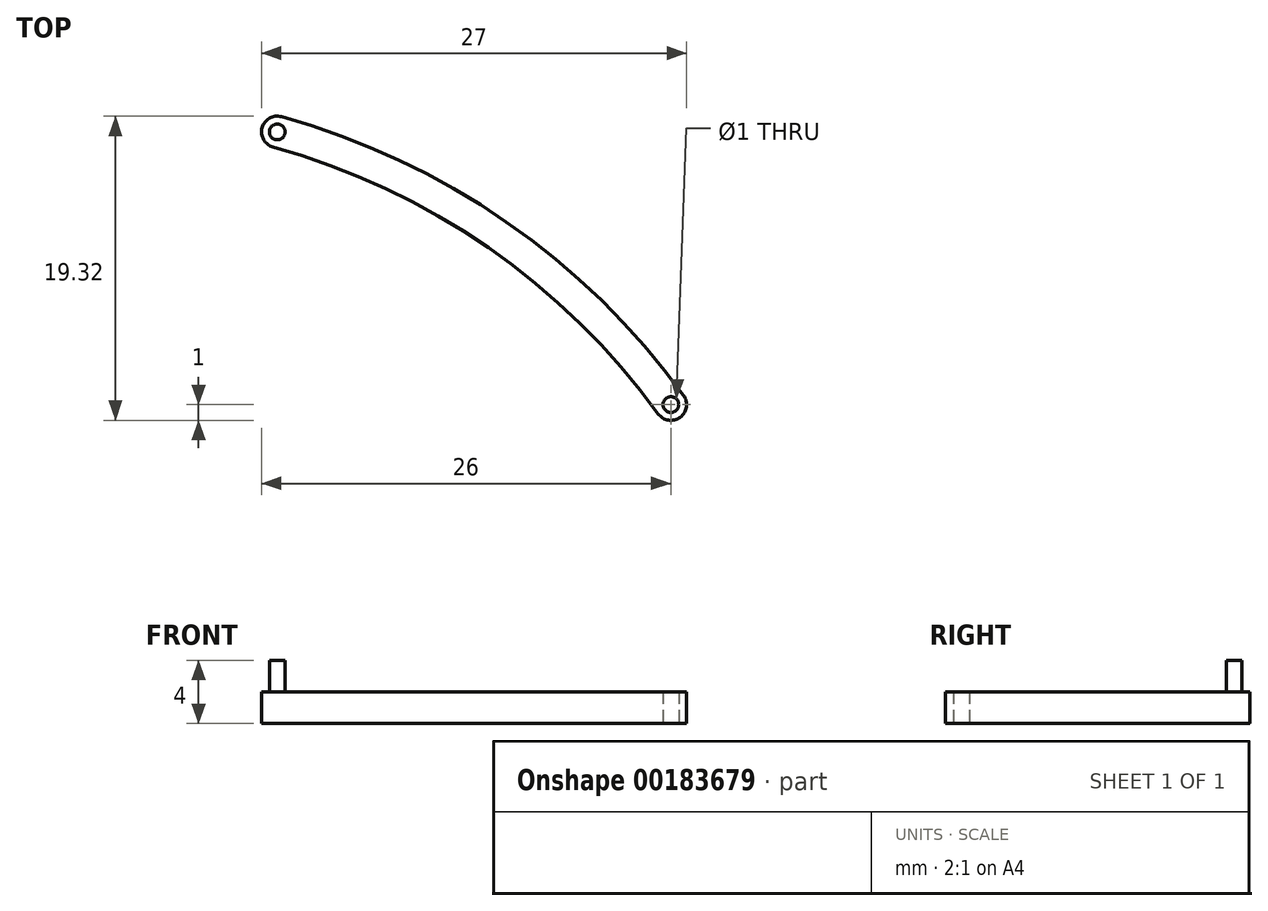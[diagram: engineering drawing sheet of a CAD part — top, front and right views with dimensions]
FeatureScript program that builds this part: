
annotation { "Feature Type Name" : "Feature", "Feature Type Description" : "" }
export const myFeature = defineFeature(function(context is Context, id is Id, definition is map)
    precondition{}
    {
        {
            var Q0;
            Q0=qCreatedBy(makeId("Top.planeOp"),FACE);
            var sketch = newSketch(context, id + "F0", { "sketchPlane" : qUnion([Q0])});
            skArc(sketch, "E0", {"start": v(14.2, -0.59) * mm, "mid": v(15.59, -0.8) * mm, "end": v(15.8, 0.59) * mm});
            skArc(sketch, "E1", {"start": v(-9.73, 18.28) * mm, "mid": v(-10.96, 17.59) * mm, "end": v(-10.27, 16.36) * mm});
            skLineSegment(sketch, "E2", {"start": v(-10, 17.32) * mm, "end": v(0, 0) * mm, "construction": true});
            skLineSegment(sketch, "E3", {"start": v(0, 0) * mm, "end": v(15, 0) * mm, "construction": true});
            skArc(sketch, "E4", {"start": v(15.8, 0.59) * mm, "mid": v(4.54, 11.6) * mm, "end": v(-9.73, 18.28) * mm});
            skArc(sketch, "E5", {"start": v(14.2, -0.59) * mm, "mid": v(3.4, 9.96) * mm, "end": v(-10.27, 16.36) * mm});
            skCircle(sketch, "E6", {"center": v(15, 0) * mm, "radius": 0.5 * mm});
            skSolve(sketch);
        }
        {
            var Q0;
            Q0 = qSketchRegion(id + "F0", true);
            extrude(context, id + "F1", {"entities" : qUnion([Q0]), "depth" : 2 * mm});
        }
        {
            var Q0;
            Q0=makeQuery(id+"F1.opExtrude","CAP_FACE",FACE,{"disambiguationData":[OSD([sQuery(id+"F0.wireOp",EDGE,"E0"),sQuery(id+"F0.wireOp",EDGE,"E1"),sQuery(id+"F0.wireOp",EDGE,"E4"),sQuery(id+"F0.wireOp",EDGE,"E5"),sQuery(id+"F0.wireOp",EDGE,"E6")])],"isStart":false});
            var sketch = newSketch(context, id + "F2", { "sketchPlane" : qUnion([Q0])});
            skCircle(sketch, "E7", {"center": v(-10, 17.32) * mm, "radius": 0.5 * mm});
            skSolve(sketch);
        }
        {
            var Q0;
            Q0 = qSketchRegion(id + "F2", true);
            extrude(context, id + "F3", {"entities" : qUnion([Q0]), "operationType" : NewBodyOperationType.ADD, "depth" : 2 * mm});
        }
    });
